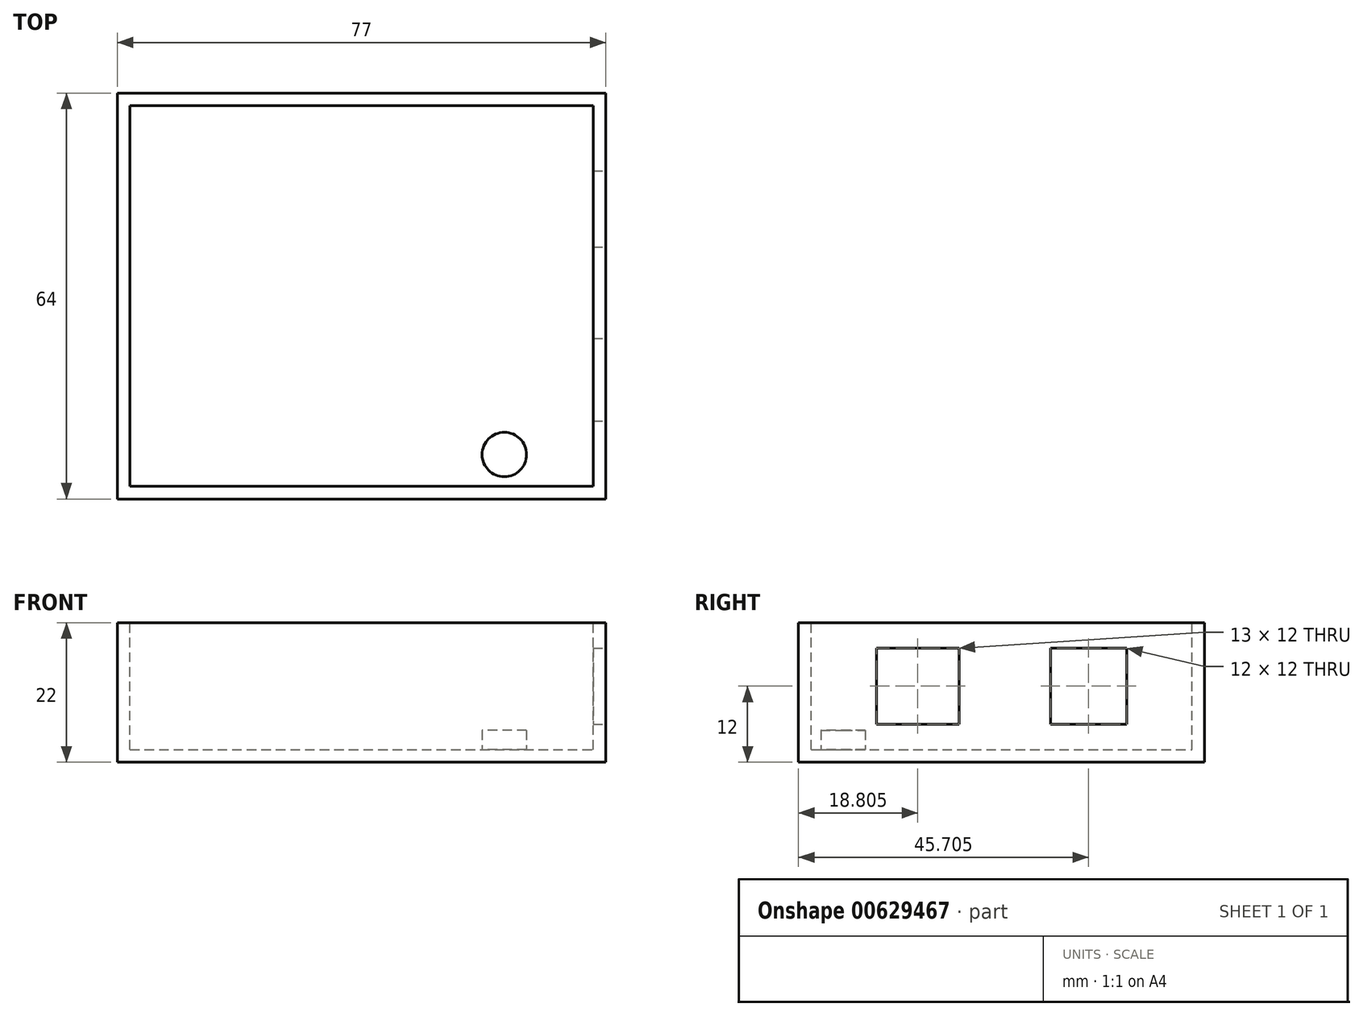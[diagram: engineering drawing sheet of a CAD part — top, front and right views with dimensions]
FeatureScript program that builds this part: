
annotation { "Feature Type Name" : "Feature", "Feature Type Description" : "" }
export const myFeature = defineFeature(function(context is Context, id is Id, definition is map)
    precondition{}
    {
        {
            assignVariable(context, id + "F0", {"name" : "h", "anyValue" : 18});
        }
        {
            assignVariable(context, id + "F1", {"name" : "t", "anyValue" : 2});
        }
        {
            var Q0;
            Q0=qCreatedBy(makeId("Top.planeOp"),FACE);
            var sketch = newSketch(context, id + "F2", { "sketchPlane" : qUnion([Q0])});
            skLineSegment(sketch, "E0.bottom", {"start": v(-35.23, 35.82) * mm, "end": v(41.77, 35.82) * mm});
            skLineSegment(sketch, "E0.top", {"start": v(-35.23, -28.18) * mm, "end": v(41.77, -28.18) * mm});
            skLineSegment(sketch, "E0.left", {"start": v(-35.23, 35.82) * mm, "end": v(-35.23, -28.18) * mm});
            skLineSegment(sketch, "E0.right", {"start": v(41.77, 35.82) * mm, "end": v(41.77, -28.18) * mm});
            skSolve(sketch);
        }
        {
            var Q0;
            Q0=makeQuery(id+"F2.imprint","IMPRINT",FACE,{"disambiguationData":[TD([[makeQuery(id+"F2.imprint","IMPRINT",EDGE,{"derivedFrom":sQuery(id+"F2.wireOp",EDGE,"E0.bottom")}),-1.0]])]});
            extrude(context, id + "F3", {"entities" : qUnion([Q0]), "depth" : (getVariable(context, 'h') + 2 * getVariable(context, 't')) * mm, "offsetDistance" : 25 * mm});
        }
        {
            var Q0;
            Q0=makeQuery(id+"F3.opExtrude","CAP_FACE",FACE,{"disambiguationData":[OSD([sQuery(id+"F2.wireOp",EDGE,"E0.bottom"),sQuery(id+"F2.wireOp",EDGE,"E0.top"),sQuery(id+"F2.wireOp",EDGE,"E0.left"),sQuery(id+"F2.wireOp",EDGE,"E0.right")])],"isStart":false});
            var sketch = newSketch(context, id + "F4", { "sketchPlane" : qUnion([Q0])});
            skLineSegment(sketch, "E1.bottom", {"start": v(-33.23, -26.18) * mm, "end": v(39.77, -26.18) * mm});
            skLineSegment(sketch, "E1.top", {"start": v(-33.23, 33.82) * mm, "end": v(39.77, 33.82) * mm});
            skLineSegment(sketch, "E1.left", {"start": v(-33.23, -26.18) * mm, "end": v(-33.23, 33.82) * mm});
            skLineSegment(sketch, "E1.right", {"start": v(39.77, -26.18) * mm, "end": v(39.77, 33.82) * mm});
            skSolve(sketch);
        }
        {
            var Q0;
            Q0=makeQuery(id+"F4.imprint","IMPRINT",FACE,{"disambiguationData":[TD([[makeQuery(id+"F4.imprint","IMPRINT",EDGE,{"derivedFrom":sQuery(id+"F4.wireOp",EDGE,"E1.bottom")}),1.0]])]});
            extrude(context, id + "F5", {"entities" : qUnion([Q0]), "operationType" : NewBodyOperationType.REMOVE, "oppositeDirection" : true, "depth" : (getVariable(context, 't') + getVariable(context, 'h')) * mm, "offsetDistance" : 25 * mm});
        }
        {
            var Q0;
            Q0=makeQuery(id+"F3.opExtrude","SWEPT_FACE",FACE,{"disambiguationData":[OSD([sQuery(id+"F2.wireOp",EDGE,"E0.right")])]});
            var sketch = newSketch(context, id + "F6", { "sketchPlane" : qUnion([Q0])});
            skLineSegment(sketch, "E2.bottom", {"start": v(-15.88, 18) * mm, "end": v(-2.88, 18) * mm});
            skLineSegment(sketch, "E2.top", {"start": v(-15.88, 6) * mm, "end": v(-2.88, 6) * mm});
            skLineSegment(sketch, "E2.left", {"start": v(-15.88, 18) * mm, "end": v(-15.88, 6) * mm});
            skLineSegment(sketch, "E2.right", {"start": v(-2.88, 18) * mm, "end": v(-2.88, 6) * mm});
            skSolve(sketch);
        }
        {
            var Q0;
            Q0=makeQuery(id+"F6.imprint","IMPRINT",FACE,{"disambiguationData":[TD([[makeQuery(id+"F6.imprint","IMPRINT",EDGE,{"derivedFrom":sQuery(id+"F6.wireOp",EDGE,"E2.bottom")}),1.0]])]});
            var sketch = newSketch(context, id + "F7", { "sketchPlane" : qUnion([Q0])});
            skLineSegment(sketch, "E3.bottom", {"start": v(11.52, 18) * mm, "end": v(23.52, 18) * mm});
            skLineSegment(sketch, "E3.top", {"start": v(11.52, 6) * mm, "end": v(23.52, 6) * mm});
            skLineSegment(sketch, "E3.left", {"start": v(11.52, 18) * mm, "end": v(11.52, 6) * mm});
            skLineSegment(sketch, "E3.right", {"start": v(23.52, 18) * mm, "end": v(23.52, 6) * mm});
            skSolve(sketch);
        }
        {
            var Q0;
            Q0 = qSketchRegion(id + "F6", true);
            extrude(context, id + "F8", {"entities" : qUnion([Q0]), "operationType" : NewBodyOperationType.REMOVE, "oppositeDirection" : true, "depth" : (getVariable(context, 't')) * mm, "offsetDistance" : 25 * mm});
        }
        {
            var Q0;
            Q0=makeQuery(id+"F7.imprint","IMPRINT",FACE,{"disambiguationData":[TD([[makeQuery(id+"F7.imprint","IMPRINT",EDGE,{"derivedFrom":sQuery(id+"F7.wireOp",EDGE,"E3.bottom")}),-1.0]])]});
            extrude(context, id + "F9", {"entities" : qUnion([Q0]), "operationType" : NewBodyOperationType.REMOVE, "oppositeDirection" : true, "depth" : (getVariable(context, 't')) * mm, "offsetDistance" : 25 * mm});
        }
        {
            var Q0;
            Q0=makeQuery(id+"F5.boolean.opBoolean","COPY",FACE,{"derivedFrom":makeQuery(id+"F5.opExtrude","CAP_FACE",FACE,{"disambiguationData":[OSD([sQuery(id+"F4.wireOp",EDGE,"E1.bottom"),sQuery(id+"F4.wireOp",EDGE,"E1.top"),sQuery(id+"F4.wireOp",EDGE,"E1.left"),sQuery(id+"F4.wireOp",EDGE,"E1.right")])],"isStart":false})});
            var sketch = newSketch(context, id + "F10", { "sketchPlane" : qUnion([Q0])});
            skCircle(sketch, "E4", {"center": v(25.77, -21.18) * mm, "radius": 3.5 * mm});
            skSolve(sketch);
        }
        {
            var Q0;
            Q0=makeQuery(id+"F10.imprint","IMPRINT",FACE,{"disambiguationData":[TD([[makeQuery(id+"F10.imprint","IMPRINT",EDGE,{"derivedFrom":sQuery(id+"F10.wireOp",EDGE,"E4")}),1.0]])]});
            extrude(context, id + "F11", {"entities" : qUnion([Q0]), "operationType" : NewBodyOperationType.ADD, "depth" : 3 * mm, "offsetDistance" : 25 * mm});
        }
    });
